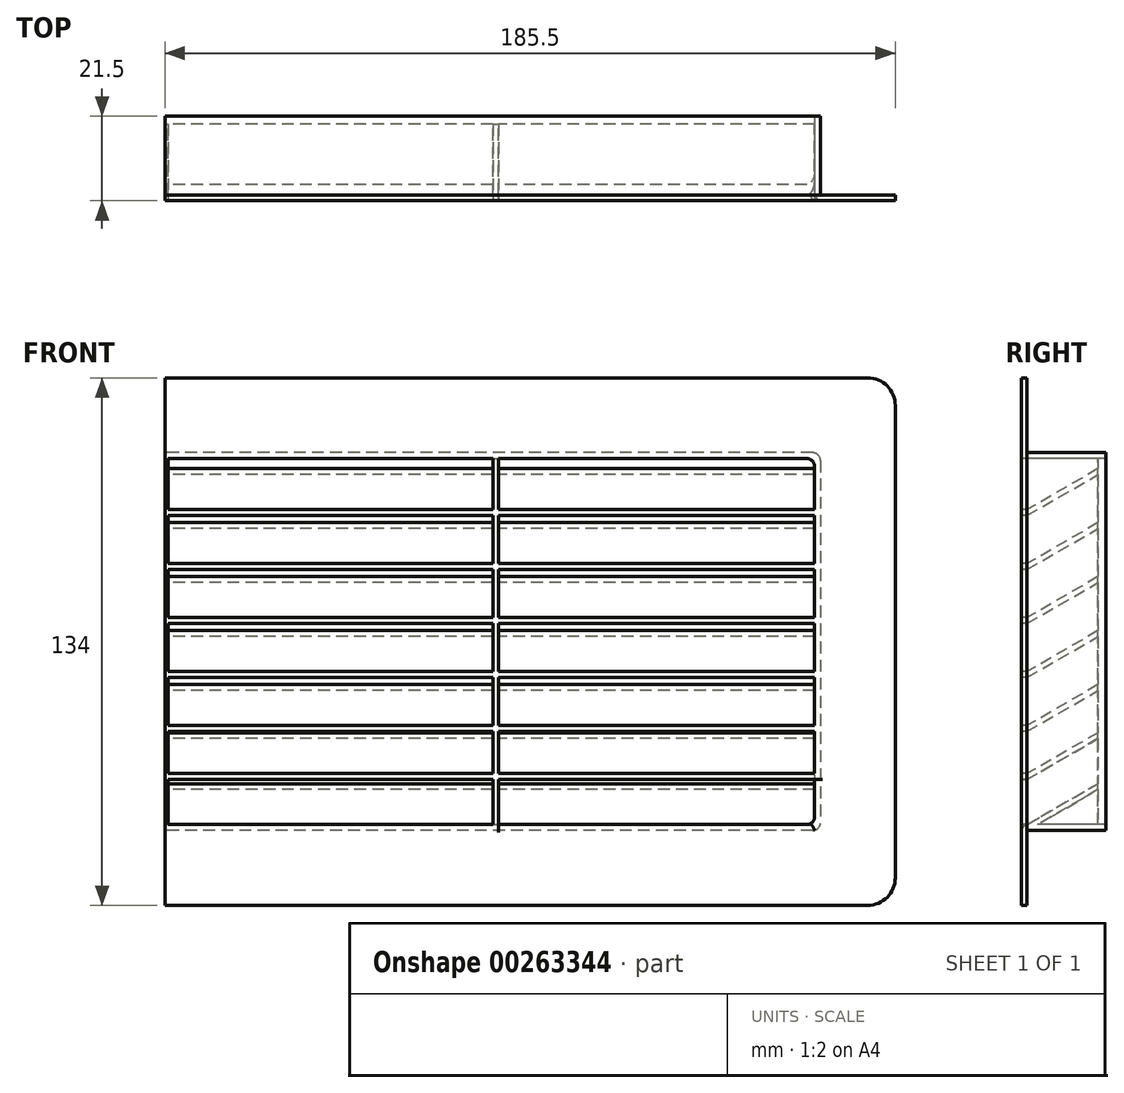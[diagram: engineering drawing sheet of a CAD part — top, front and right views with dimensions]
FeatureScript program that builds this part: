
annotation { "Feature Type Name" : "Feature", "Feature Type Description" : "" }
export const myFeature = defineFeature(function(context is Context, id is Id, definition is map)
    precondition{}
    {
        {
            var Q0;
            Q0=qCreatedBy(makeId("Front.planeOp"),FACE);
            var sketch = newSketch(context, id + "F0", { "sketchPlane" : qUnion([Q0])});
            skLineSegment(sketch, "E0.bottom", {"start": v(-180, 65) * mm, "end": v(180, 65) * mm});
            skLineSegment(sketch, "E0.top", {"start": v(-180, -65) * mm, "end": v(180, -65) * mm});
            skLineSegment(sketch, "E0.left", {"start": v(-185, 60) * mm, "end": v(-185, -60) * mm});
            skLineSegment(sketch, "E0.right", {"start": v(185, 60) * mm, "end": v(185, -60) * mm});
            skPoint(sketch, "E0.middle", {"position": v(0, 0) * mm});
            skPoint(sketch, "E1.visualSharp", {"position": v(-185, 65) * mm});
            skArc(sketch, "E1.filletArc", {"start": v(-180, 65) * mm, "mid": v(-183.54, 63.54) * mm, "end": v(-185, 60) * mm});
            skPoint(sketch, "E2.visualSharp", {"position": v(185, 65) * mm});
            skArc(sketch, "E2.filletArc", {"start": v(185, 60) * mm, "mid": v(183.54, 63.54) * mm, "end": v(180, 65) * mm});
            skPoint(sketch, "E3.visualSharp", {"position": v(185, -65) * mm});
            skArc(sketch, "E3.filletArc", {"start": v(180, -65) * mm, "mid": v(183.54, -63.54) * mm, "end": v(185, -60) * mm});
            skPoint(sketch, "E4.visualSharp", {"position": v(-185, -65) * mm});
            skArc(sketch, "E4.filletArc", {"start": v(-185, -60) * mm, "mid": v(-183.54, -63.54) * mm, "end": v(-180, -65) * mm});
            skSolve(sketch);
        }
        {
            var Q0;
            Q0=qSketchRegion(id+"F0",true);
            extrude(context, id + "F1", {"entities" : qUnion([Q0]), "depth" : 1.5 * mm});
        }
        {
            var Q0;
            Q0=makeQuery(id+"F1.opExtrude","CAP_FACE",FACE,{"disambiguationData":[OSD([sQuery(id+"F0.wireOp",EDGE,"E0.bottom"),sQuery(id+"F0.wireOp",EDGE,"E0.top"),sQuery(id+"F0.wireOp",EDGE,"E0.left"),sQuery(id+"F0.wireOp",EDGE,"E0.right")])],"isStart":false});
            var sketch = newSketch(context, id + "F2", { "sketchPlane" : qUnion([Q0])});
            skLineSegment(sketch, "E5.bottom", {"start": v(-166.5, 46.5) * mm, "end": v(-83.25, 46.5) * mm});
            skLineSegment(sketch, "E5.top", {"start": v(-166.5, -46.5) * mm, "end": v(-83.25, -46.5) * mm});
            skLineSegment(sketch, "E5.left", {"start": v(-166.5, 46.5) * mm, "end": v(-166.5, 33.54) * mm});
            skLineSegment(sketch, "E5.right", {"start": v(166.5, 46.5) * mm, "end": v(166.5, 33.54) * mm});
            skPoint(sketch, "E5.middle", {"position": v(0, 0) * mm});
            skLineSegment(sketch, "E6.0", {"start": v(-166.5, 32.04) * mm, "end": v(-83.25, 32.04) * mm});
            skLineSegment(sketch, "E7.0", {"start": v(-166.5, 18.32) * mm, "end": v(-83.25, 18.32) * mm});
            skLineSegment(sketch, "E8.0", {"start": v(-166.5, 4.6) * mm, "end": v(-83.25, 4.6) * mm});
            skLineSegment(sketch, "E9.0", {"start": v(-166.5, -9.1) * mm, "end": v(-83.25, -9.1) * mm});
            skLineSegment(sketch, "E10.0", {"start": v(-166.5, -22.82) * mm, "end": v(-83.25, -22.82) * mm});
            skLineSegment(sketch, "E11.0", {"start": v(-166.5, -33.54) * mm, "end": v(-83.25, -33.54) * mm});
            skLineSegment(sketch, "E12.0", {"start": v(-166.5, 33.54) * mm, "end": v(-83.25, 33.54) * mm});
            skLineSegment(sketch, "E13.0", {"start": v(-166.5, 19.82) * mm, "end": v(-83.25, 19.82) * mm});
            skLineSegment(sketch, "E14.0", {"start": v(-166.5, 6.1) * mm, "end": v(-83.25, 6.1) * mm});
            skLineSegment(sketch, "E15.0", {"start": v(-166.5, -7.6) * mm, "end": v(-83.25, -7.6) * mm});
            skLineSegment(sketch, "E16.0", {"start": v(-166.5, -21.32) * mm, "end": v(-83.25, -21.32) * mm});
            skLineSegment(sketch, "E17.0", {"start": v(-166.5, -35.04) * mm, "end": v(-83.25, -35.04) * mm});
            skLineSegment(sketch, "E18.0", {"start": v(-83.25, 46.5) * mm, "end": v(-83.25, 33.54) * mm});
            skLineSegment(sketch, "E19.0", {"start": v(-81.75, 46.5) * mm, "end": v(-81.75, 33.54) * mm});
            skLineSegment(sketch, "E20.0", {"start": v(0.75, 46.5) * mm, "end": v(0.75, 33.54) * mm});
            skLineSegment(sketch, "E21.0", {"start": v(2.25, 46.5) * mm, "end": v(2.25, 33.54) * mm});
            skLineSegment(sketch, "E22.0", {"start": v(84.75, 46.5) * mm, "end": v(84.75, 33.54) * mm});
            skLineSegment(sketch, "E23.0", {"start": v(86.25, 46.5) * mm, "end": v(86.25, 33.54) * mm});
            skLineSegment(sketch, "E24.trimOffspring", {"start": v(-81.75, 19.82) * mm, "end": v(0.75, 19.82) * mm});
            skLineSegment(sketch, "E25.trimOffspring", {"start": v(-81.75, 18.32) * mm, "end": v(0.75, 18.32) * mm});
            skLineSegment(sketch, "E26.trimOffspring", {"start": v(-81.75, 33.54) * mm, "end": v(0.75, 33.54) * mm});
            skLineSegment(sketch, "E27.trimOffspring", {"start": v(-81.75, 32.04) * mm, "end": v(0.75, 32.04) * mm});
            skLineSegment(sketch, "E28.trimOffspring", {"start": v(-83.25, 32.04) * mm, "end": v(-83.25, 19.82) * mm});
            skLineSegment(sketch, "E29.trimOffspring", {"start": v(-81.75, 32.04) * mm, "end": v(-81.75, 19.82) * mm});
            skLineSegment(sketch, "E30.trimOffspring", {"start": v(-166.5, 32.04) * mm, "end": v(-166.5, 19.82) * mm});
            skLineSegment(sketch, "E31.trimOffspring", {"start": v(-166.5, 18.32) * mm, "end": v(-166.5, 6.1) * mm});
            skLineSegment(sketch, "E32.trimOffspring", {"start": v(-81.75, 18.32) * mm, "end": v(-81.75, 6.1) * mm});
            skLineSegment(sketch, "E33.trimOffspring", {"start": v(-83.25, 18.32) * mm, "end": v(-83.25, 6.1) * mm});
            skLineSegment(sketch, "E34.trimOffspring", {"start": v(-83.25, 4.6) * mm, "end": v(-83.25, -7.6) * mm});
            skLineSegment(sketch, "E35.trimOffspring", {"start": v(-81.75, 4.6) * mm, "end": v(-81.75, -7.6) * mm});
            skLineSegment(sketch, "E36.trimOffspring", {"start": v(-81.75, 4.6) * mm, "end": v(0.75, 4.6) * mm});
            skLineSegment(sketch, "E37.trimOffspring", {"start": v(-81.75, 6.1) * mm, "end": v(0.75, 6.1) * mm});
            skLineSegment(sketch, "E38.trimOffspring", {"start": v(-166.5, 4.6) * mm, "end": v(-166.5, -7.6) * mm});
            skLineSegment(sketch, "E39.trimOffspring", {"start": v(-166.5, -9.1) * mm, "end": v(-166.5, -21.32) * mm});
            skLineSegment(sketch, "E40.trimOffspring", {"start": v(-83.25, -9.1) * mm, "end": v(-83.25, -21.32) * mm});
            skLineSegment(sketch, "E41.trimOffspring", {"start": v(-81.75, -9.1) * mm, "end": v(-81.75, -21.32) * mm});
            skLineSegment(sketch, "E42.trimOffspring", {"start": v(-81.75, -7.6) * mm, "end": v(0.75, -7.6) * mm});
            skLineSegment(sketch, "E43.trimOffspring", {"start": v(-81.75, -9.1) * mm, "end": v(0.75, -9.1) * mm});
            skLineSegment(sketch, "E44.trimOffspring", {"start": v(-166.5, -22.82) * mm, "end": v(-166.5, -33.54) * mm});
            skLineSegment(sketch, "E45.trimOffspring", {"start": v(-166.5, -35.04) * mm, "end": v(-166.5, -46.5) * mm});
            skLineSegment(sketch, "E46.trimOffspring", {"start": v(-83.25, -22.82) * mm, "end": v(-83.25, -33.54) * mm});
            skLineSegment(sketch, "E47.trimOffspring", {"start": v(-81.75, -22.82) * mm, "end": v(0.75, -22.82) * mm});
            skLineSegment(sketch, "E48.trimOffspring", {"start": v(-81.75, -21.32) * mm, "end": v(0.75, -21.32) * mm});
            skLineSegment(sketch, "E49.trimOffspring", {"start": v(-81.75, -22.82) * mm, "end": v(-81.75, -33.54) * mm});
            skLineSegment(sketch, "E50.trimOffspring", {"start": v(-83.25, -35.04) * mm, "end": v(-83.25, -46.5) * mm});
            skLineSegment(sketch, "E51.trimOffspring", {"start": v(-81.75, -35.04) * mm, "end": v(0.75, -35.04) * mm});
            skLineSegment(sketch, "E52.trimOffspring", {"start": v(-81.75, -33.54) * mm, "end": v(0.75, -33.54) * mm});
            skLineSegment(sketch, "E53.trimOffspring", {"start": v(-81.75, -35.04) * mm, "end": v(-81.75, -46.5) * mm});
            skLineSegment(sketch, "E54.trimOffspring", {"start": v(-81.75, -46.5) * mm, "end": v(0.75, -46.5) * mm});
            skLineSegment(sketch, "E55.trimOffspring", {"start": v(-81.75, 46.5) * mm, "end": v(0.75, 46.5) * mm});
            skLineSegment(sketch, "E56.trimOffspring", {"start": v(2.25, 46.5) * mm, "end": v(84.75, 46.5) * mm});
            skLineSegment(sketch, "E57.trimOffspring", {"start": v(2.25, 32.04) * mm, "end": v(84.75, 32.04) * mm});
            skLineSegment(sketch, "E58.trimOffspring", {"start": v(2.25, 33.54) * mm, "end": v(84.75, 33.54) * mm});
            skLineSegment(sketch, "E59.trimOffspring", {"start": v(2.25, 32.04) * mm, "end": v(2.25, 19.82) * mm});
            skLineSegment(sketch, "E60.trimOffspring", {"start": v(0.75, 32.04) * mm, "end": v(0.75, 19.82) * mm});
            skLineSegment(sketch, "E61.trimOffspring", {"start": v(2.25, 19.82) * mm, "end": v(84.75, 19.82) * mm});
            skLineSegment(sketch, "E62.trimOffspring", {"start": v(2.25, 18.32) * mm, "end": v(2.25, 6.1) * mm});
            skLineSegment(sketch, "E63.trimOffspring", {"start": v(2.25, 18.32) * mm, "end": v(84.75, 18.32) * mm});
            skLineSegment(sketch, "E64.trimOffspring", {"start": v(0.75, 18.32) * mm, "end": v(0.75, 6.1) * mm});
            skLineSegment(sketch, "E65.trimOffspring", {"start": v(2.25, 4.6) * mm, "end": v(2.25, -7.6) * mm});
            skLineSegment(sketch, "E66.trimOffspring", {"start": v(2.25, 6.1) * mm, "end": v(84.75, 6.1) * mm});
            skLineSegment(sketch, "E67.trimOffspring", {"start": v(0.75, 4.6) * mm, "end": v(0.75, -7.6) * mm});
            skLineSegment(sketch, "E68.trimOffspring", {"start": v(2.25, 4.6) * mm, "end": v(84.75, 4.6) * mm});
            skLineSegment(sketch, "E69.trimOffspring", {"start": v(2.25, -7.6) * mm, "end": v(84.75, -7.6) * mm});
            skLineSegment(sketch, "E70.trimOffspring", {"start": v(0.75, -9.1) * mm, "end": v(0.75, -21.32) * mm});
            skLineSegment(sketch, "E71.trimOffspring", {"start": v(2.25, -9.1) * mm, "end": v(2.25, -21.32) * mm});
            skLineSegment(sketch, "E72.trimOffspring", {"start": v(2.25, -9.1) * mm, "end": v(84.75, -9.1) * mm});
            skLineSegment(sketch, "E73.trimOffspring", {"start": v(2.25, -22.82) * mm, "end": v(2.25, -33.54) * mm});
            skLineSegment(sketch, "E74.trimOffspring", {"start": v(2.25, -21.32) * mm, "end": v(84.75, -21.32) * mm});
            skLineSegment(sketch, "E75.trimOffspring", {"start": v(0.75, -22.82) * mm, "end": v(0.75, -33.54) * mm});
            skLineSegment(sketch, "E76.trimOffspring", {"start": v(2.25, -22.82) * mm, "end": v(84.75, -22.82) * mm});
            skLineSegment(sketch, "E77.trimOffspring", {"start": v(2.25, -35.04) * mm, "end": v(84.75, -35.04) * mm});
            skLineSegment(sketch, "E78.trimOffspring", {"start": v(2.25, -35.04) * mm, "end": v(2.25, -46.5) * mm});
            skLineSegment(sketch, "E79.trimOffspring", {"start": v(2.25, -33.54) * mm, "end": v(84.75, -33.54) * mm});
            skLineSegment(sketch, "E80.trimOffspring", {"start": v(0.75, -35.04) * mm, "end": v(0.75, -46.5) * mm});
            skLineSegment(sketch, "E81.trimOffspring", {"start": v(2.25, -46.5) * mm, "end": v(84.75, -46.5) * mm});
            skLineSegment(sketch, "E82.trimOffspring", {"start": v(86.25, 46.5) * mm, "end": v(166.5, 46.5) * mm});
            skLineSegment(sketch, "E83.trimOffspring", {"start": v(86.25, 33.54) * mm, "end": v(166.5, 33.54) * mm});
            skLineSegment(sketch, "E84.trimOffspring", {"start": v(84.75, 32.04) * mm, "end": v(84.75, 19.82) * mm});
            skLineSegment(sketch, "E85.trimOffspring", {"start": v(86.25, 32.04) * mm, "end": v(86.25, 19.82) * mm});
            skLineSegment(sketch, "E86.trimOffspring", {"start": v(86.25, 32.04) * mm, "end": v(166.5, 32.04) * mm});
            skLineSegment(sketch, "E87.trimOffspring", {"start": v(84.75, 4.6) * mm, "end": v(84.75, -7.6) * mm});
            skLineSegment(sketch, "E88.trimOffspring", {"start": v(86.25, 4.6) * mm, "end": v(86.25, -7.6) * mm});
            skLineSegment(sketch, "E89.trimOffspring", {"start": v(86.25, 6.1) * mm, "end": v(166.5, 6.1) * mm});
            skLineSegment(sketch, "E90.trimOffspring", {"start": v(86.25, 4.6) * mm, "end": v(166.5, 4.6) * mm});
            skLineSegment(sketch, "E91.trimOffspring", {"start": v(86.25, 18.32) * mm, "end": v(166.5, 18.32) * mm});
            skLineSegment(sketch, "E92.trimOffspring", {"start": v(86.25, 18.32) * mm, "end": v(86.25, 6.1) * mm});
            skLineSegment(sketch, "E93.trimOffspring", {"start": v(84.75, 18.32) * mm, "end": v(84.75, 6.1) * mm});
            skLineSegment(sketch, "E94.trimOffspring", {"start": v(86.25, 19.82) * mm, "end": v(166.5, 19.82) * mm});
            skLineSegment(sketch, "E95.trimOffspring", {"start": v(86.25, -22.82) * mm, "end": v(166.5, -22.82) * mm});
            skLineSegment(sketch, "E96.trimOffspring", {"start": v(86.25, -22.82) * mm, "end": v(86.25, -33.54) * mm});
            skLineSegment(sketch, "E97.trimOffspring", {"start": v(84.75, -22.82) * mm, "end": v(84.75, -33.54) * mm});
            skLineSegment(sketch, "E98.trimOffspring", {"start": v(86.25, -9.1) * mm, "end": v(86.25, -21.32) * mm});
            skLineSegment(sketch, "E99.trimOffspring", {"start": v(84.75, -9.1) * mm, "end": v(84.75, -21.32) * mm});
            skLineSegment(sketch, "E100.trimOffspring", {"start": v(86.25, -7.6) * mm, "end": v(166.5, -7.6) * mm});
            skLineSegment(sketch, "E101.trimOffspring", {"start": v(86.25, -9.1) * mm, "end": v(166.5, -9.1) * mm});
            skLineSegment(sketch, "E102.trimOffspring", {"start": v(86.25, -21.32) * mm, "end": v(166.5, -21.32) * mm});
            skLineSegment(sketch, "E103.trimOffspring", {"start": v(86.25, -35.04) * mm, "end": v(86.25, -46.5) * mm});
            skLineSegment(sketch, "E104.trimOffspring", {"start": v(86.25, -35.04) * mm, "end": v(166.5, -35.04) * mm});
            skLineSegment(sketch, "E105.trimOffspring", {"start": v(86.25, -33.54) * mm, "end": v(166.5, -33.54) * mm});
            skLineSegment(sketch, "E106.trimOffspring", {"start": v(84.75, -35.04) * mm, "end": v(84.75, -46.5) * mm});
            skLineSegment(sketch, "E107.trimOffspring", {"start": v(86.25, -46.5) * mm, "end": v(166.5, -46.5) * mm});
            skLineSegment(sketch, "E108.trimOffspring", {"start": v(166.5, -35.04) * mm, "end": v(166.5, -46.5) * mm});
            skLineSegment(sketch, "E109.trimOffspring", {"start": v(166.5, -22.82) * mm, "end": v(166.5, -33.54) * mm});
            skLineSegment(sketch, "E110.trimOffspring", {"start": v(166.5, 32.04) * mm, "end": v(166.5, 19.82) * mm});
            skLineSegment(sketch, "E111.trimOffspring", {"start": v(166.5, 18.32) * mm, "end": v(166.5, 6.1) * mm});
            skLineSegment(sketch, "E112.trimOffspring", {"start": v(166.5, 4.6) * mm, "end": v(166.5, -7.6) * mm});
            skLineSegment(sketch, "E113.trimOffspring", {"start": v(166.5, -9.1) * mm, "end": v(166.5, -21.32) * mm});
            skSolve(sketch);
        }
        {
            var Q0;
            Q0=makeQuery(id+"F2.imprint","IMPRINT",FACE,{"disambiguationData":[TD([[makeQuery(id+"F2.imprint","IMPRINT",EDGE,{"derivedFrom":sQuery(id+"F2.wireOp",EDGE,"E5.bottom")}),-1.0]])]});
            var Q1;
            Q1=makeQuery(id+"F2.imprint","IMPRINT",FACE,{"disambiguationData":[TD([[makeQuery(id+"F2.imprint","IMPRINT",EDGE,{"derivedFrom":sQuery(id+"F2.wireOp",EDGE,"E19.0")}),1.0]])]});
            var Q2;
            Q2=makeQuery(id+"F2.imprint","IMPRINT",FACE,{"disambiguationData":[TD([[makeQuery(id+"F2.imprint","IMPRINT",EDGE,{"derivedFrom":sQuery(id+"F2.wireOp",EDGE,"E21.0")}),1.0]])]});
            var Q3;
            Q3=makeQuery(id+"F2.imprint","IMPRINT",FACE,{"disambiguationData":[TD([[makeQuery(id+"F2.imprint","IMPRINT",EDGE,{"derivedFrom":sQuery(id+"F2.wireOp",EDGE,"E5.right")}),-1.0]])]});
            var Q4;
            Q4=makeQuery(id+"F2.imprint","IMPRINT",FACE,{"disambiguationData":[TD([[makeQuery(id+"F2.imprint","IMPRINT",EDGE,{"derivedFrom":sQuery(id+"F2.wireOp",EDGE,"E6.0")}),-1.0]])]});
            var Q5;
            Q5=makeQuery(id+"F2.imprint","IMPRINT",FACE,{"disambiguationData":[TD([[makeQuery(id+"F2.imprint","IMPRINT",EDGE,{"derivedFrom":sQuery(id+"F2.wireOp",EDGE,"E24.trimOffspring")}),1.0]])]});
            var Q6;
            Q6=makeQuery(id+"F2.imprint","IMPRINT",FACE,{"disambiguationData":[TD([[makeQuery(id+"F2.imprint","IMPRINT",EDGE,{"derivedFrom":sQuery(id+"F2.wireOp",EDGE,"E57.trimOffspring")}),-1.0]])]});
            var Q7;
            Q7=makeQuery(id+"F2.imprint","IMPRINT",FACE,{"disambiguationData":[TD([[makeQuery(id+"F2.imprint","IMPRINT",EDGE,{"derivedFrom":sQuery(id+"F2.wireOp",EDGE,"E85.trimOffspring")}),1.0]])]});
            var Q8;
            Q8=makeQuery(id+"F2.imprint","IMPRINT",FACE,{"disambiguationData":[TD([[makeQuery(id+"F2.imprint","IMPRINT",EDGE,{"derivedFrom":sQuery(id+"F2.wireOp",EDGE,"E7.0")}),-1.0]])]});
            var Q9;
            Q9=makeQuery(id+"F2.imprint","IMPRINT",FACE,{"disambiguationData":[TD([[makeQuery(id+"F2.imprint","IMPRINT",EDGE,{"derivedFrom":sQuery(id+"F2.wireOp",EDGE,"E25.trimOffspring")}),-1.0]])]});
            var Q10;
            Q10=makeQuery(id+"F2.imprint","IMPRINT",FACE,{"disambiguationData":[TD([[makeQuery(id+"F2.imprint","IMPRINT",EDGE,{"derivedFrom":sQuery(id+"F2.wireOp",EDGE,"E62.trimOffspring")}),1.0]])]});
            var Q11;
            Q11=makeQuery(id+"F2.imprint","IMPRINT",FACE,{"disambiguationData":[TD([[makeQuery(id+"F2.imprint","IMPRINT",EDGE,{"derivedFrom":sQuery(id+"F2.wireOp",EDGE,"E89.trimOffspring")}),1.0]])]});
            var Q12;
            Q12=makeQuery(id+"F2.imprint","IMPRINT",FACE,{"disambiguationData":[TD([[makeQuery(id+"F2.imprint","IMPRINT",EDGE,{"derivedFrom":sQuery(id+"F2.wireOp",EDGE,"E8.0")}),-1.0]])]});
            var Q13;
            Q13=makeQuery(id+"F2.imprint","IMPRINT",FACE,{"disambiguationData":[TD([[makeQuery(id+"F2.imprint","IMPRINT",EDGE,{"derivedFrom":sQuery(id+"F2.wireOp",EDGE,"E35.trimOffspring")}),1.0]])]});
            var Q14;
            Q14=makeQuery(id+"F2.imprint","IMPRINT",FACE,{"disambiguationData":[TD([[makeQuery(id+"F2.imprint","IMPRINT",EDGE,{"derivedFrom":sQuery(id+"F2.wireOp",EDGE,"E65.trimOffspring")}),1.0]])]});
            var Q15;
            Q15=makeQuery(id+"F2.imprint","IMPRINT",FACE,{"disambiguationData":[TD([[makeQuery(id+"F2.imprint","IMPRINT",EDGE,{"derivedFrom":sQuery(id+"F2.wireOp",EDGE,"E88.trimOffspring")}),1.0]])]});
            var Q16;
            Q16=makeQuery(id+"F2.imprint","IMPRINT",FACE,{"disambiguationData":[TD([[makeQuery(id+"F2.imprint","IMPRINT",EDGE,{"derivedFrom":sQuery(id+"F2.wireOp",EDGE,"E9.0")}),-1.0]])]});
            var Q17;
            Q17=makeQuery(id+"F2.imprint","IMPRINT",FACE,{"disambiguationData":[TD([[makeQuery(id+"F2.imprint","IMPRINT",EDGE,{"derivedFrom":sQuery(id+"F2.wireOp",EDGE,"E41.trimOffspring")}),1.0]])]});
            var Q18;
            Q18=makeQuery(id+"F2.imprint","IMPRINT",FACE,{"disambiguationData":[TD([[makeQuery(id+"F2.imprint","IMPRINT",EDGE,{"derivedFrom":sQuery(id+"F2.wireOp",EDGE,"E71.trimOffspring")}),1.0]])]});
            var Q19;
            Q19=makeQuery(id+"F2.imprint","IMPRINT",FACE,{"disambiguationData":[TD([[makeQuery(id+"F2.imprint","IMPRINT",EDGE,{"derivedFrom":sQuery(id+"F2.wireOp",EDGE,"E98.trimOffspring")}),1.0]])]});
            var Q20;
            Q20=makeQuery(id+"F2.imprint","IMPRINT",FACE,{"disambiguationData":[TD([[makeQuery(id+"F2.imprint","IMPRINT",EDGE,{"derivedFrom":sQuery(id+"F2.wireOp",EDGE,"E10.0")}),-1.0]])]});
            var Q21;
            Q21=makeQuery(id+"F2.imprint","IMPRINT",FACE,{"disambiguationData":[TD([[makeQuery(id+"F2.imprint","IMPRINT",EDGE,{"derivedFrom":sQuery(id+"F2.wireOp",EDGE,"E47.trimOffspring")}),-1.0]])]});
            var Q22;
            Q22=makeQuery(id+"F2.imprint","IMPRINT",FACE,{"disambiguationData":[TD([[makeQuery(id+"F2.imprint","IMPRINT",EDGE,{"derivedFrom":sQuery(id+"F2.wireOp",EDGE,"E73.trimOffspring")}),1.0]])]});
            var Q23;
            Q23=makeQuery(id+"F2.imprint","IMPRINT",FACE,{"disambiguationData":[TD([[makeQuery(id+"F2.imprint","IMPRINT",EDGE,{"derivedFrom":sQuery(id+"F2.wireOp",EDGE,"E95.trimOffspring")}),-1.0]])]});
            var Q24;
            Q24=makeQuery(id+"F2.imprint","IMPRINT",FACE,{"disambiguationData":[TD([[makeQuery(id+"F2.imprint","IMPRINT",EDGE,{"derivedFrom":sQuery(id+"F2.wireOp",EDGE,"E5.top")}),1.0]])]});
            var Q25;
            Q25=makeQuery(id+"F2.imprint","IMPRINT",FACE,{"disambiguationData":[TD([[makeQuery(id+"F2.imprint","IMPRINT",EDGE,{"derivedFrom":sQuery(id+"F2.wireOp",EDGE,"E51.trimOffspring")}),-1.0]])]});
            var Q26;
            Q26=makeQuery(id+"F2.imprint","IMPRINT",FACE,{"disambiguationData":[TD([[makeQuery(id+"F2.imprint","IMPRINT",EDGE,{"derivedFrom":sQuery(id+"F2.wireOp",EDGE,"E77.trimOffspring")}),-1.0]])]});
            var Q27;
            Q27=makeQuery(id+"F2.imprint","IMPRINT",FACE,{"disambiguationData":[TD([[makeQuery(id+"F2.imprint","IMPRINT",EDGE,{"derivedFrom":sQuery(id+"F2.wireOp",EDGE,"E103.trimOffspring")}),1.0]])]});
            extrude(context, id + "F3", {"entities" : qUnion([Q0, Q1, Q2, Q3, Q4, Q5, Q6, Q7, Q8, Q9, Q10, Q11, Q12, Q13, Q14, Q15, Q16, Q17, Q18, Q19, Q20, Q21, Q22, Q23, Q24, Q25, Q26, Q27]), "operationType" : NewBodyOperationType.REMOVE, "endBound" : BoundingType.THROUGH_ALL, "oppositeDirection" : true, "depth" : 25 * mm});
        }
        {
            var Q0;
            Q0=makeQuery(id+"F1.opExtrude","CAP_FACE",FACE,{"disambiguationData":[OSD([sQuery(id+"F0.wireOp",EDGE,"E0.bottom"),sQuery(id+"F0.wireOp",EDGE,"E0.top"),sQuery(id+"F0.wireOp",EDGE,"E0.left"),sQuery(id+"F0.wireOp",EDGE,"E0.right")])],"isStart":true});
            var sketch = newSketch(context, id + "F4", { "sketchPlane" : qUnion([Q0])});
            skLineSegment(sketch, "E114.bottom", {"start": v(-166.5, 46.5) * mm, "end": v(166.5, 46.5) * mm});
            skLineSegment(sketch, "E114.top", {"start": v(-166.5, -46.5) * mm, "end": v(166.5, -46.5) * mm});
            skLineSegment(sketch, "E114.left", {"start": v(-166.5, 46.5) * mm, "end": v(-166.5, -46.5) * mm});
            skLineSegment(sketch, "E114.right", {"start": v(166.5, 46.5) * mm, "end": v(166.5, -46.5) * mm});
            skPoint(sketch, "E114.middle", {"position": v(0, 0) * mm});
            skLineSegment(sketch, "E115.0", {"start": v(-168, 48) * mm, "end": v(168, 48) * mm});
            skLineSegment(sketch, "E115.1", {"start": v(-168, 48) * mm, "end": v(-168, -48) * mm});
            skLineSegment(sketch, "E115.2", {"start": v(-168, -48) * mm, "end": v(168, -48) * mm});
            skLineSegment(sketch, "E115.3", {"start": v(168, 48) * mm, "end": v(168, -48) * mm});
            skSolve(sketch);
        }
        {
            var Q0;
            Q0=qSketchRegion(id+"F4",true);
            extrude(context, id + "F5", {"entities" : qUnion([Q0]), "operationType" : NewBodyOperationType.ADD, "depth" : 20 * mm});
        }
        {
            var Q0;
            Q0=makeQuery(id+"F5.boolean.opBoolean","MERGE",FACE,{"derivedFrom":[makeQuery(id+"F3.boolean.opBoolean","COPY",FACE,{"derivedFrom":makeQuery(id+"F3.opExtrude","SWEPT_FACE",FACE,{"disambiguationData":[OSD([sQuery(id+"F2.wireOp",EDGE,"E5.left")])]})}),makeQuery(id+"F3.boolean.opBoolean","COPY",FACE,{"derivedFrom":makeQuery(id+"F3.opExtrude","SWEPT_FACE",FACE,{"disambiguationData":[OSD([sQuery(id+"F2.wireOp",EDGE,"E30.trimOffspring")])]})}),makeQuery(id+"F3.boolean.opBoolean","COPY",FACE,{"derivedFrom":makeQuery(id+"F3.opExtrude","SWEPT_FACE",FACE,{"disambiguationData":[OSD([sQuery(id+"F2.wireOp",EDGE,"E31.trimOffspring")])]})}),makeQuery(id+"F3.boolean.opBoolean","COPY",FACE,{"derivedFrom":makeQuery(id+"F3.opExtrude","SWEPT_FACE",FACE,{"disambiguationData":[OSD([sQuery(id+"F2.wireOp",EDGE,"E38.trimOffspring")])]})}),makeQuery(id+"F3.boolean.opBoolean","COPY",FACE,{"derivedFrom":makeQuery(id+"F3.opExtrude","SWEPT_FACE",FACE,{"disambiguationData":[OSD([sQuery(id+"F2.wireOp",EDGE,"E39.trimOffspring")])]})}),makeQuery(id+"F3.boolean.opBoolean","COPY",FACE,{"derivedFrom":makeQuery(id+"F3.opExtrude","SWEPT_FACE",FACE,{"disambiguationData":[OSD([sQuery(id+"F2.wireOp",EDGE,"E44.trimOffspring")])]})}),makeQuery(id+"F3.boolean.opBoolean","COPY",FACE,{"derivedFrom":makeQuery(id+"F3.opExtrude","SWEPT_FACE",FACE,{"disambiguationData":[OSD([sQuery(id+"F2.wireOp",EDGE,"E45.trimOffspring")])]})}),makeQuery(id+"F5.opExtrude","SWEPT_FACE",FACE,{"disambiguationData":[OSD([sQuery(id+"F4.wireOp",EDGE,"E114.right")])]})]});
            var sketch = newSketch(context, id + "F6", { "sketchPlane" : qUnion([Q0])});
            skLineSegment(sketch, "E116", {"start": v(0, 46.5) * mm, "end": v(0, -35.04) * mm, "construction": true});
            skPoint(sketch, "E116.endSnap0", {"position": v(0, 19.07) * mm});
            skLineSegment(sketch, "E117", {"start": v(0, 33.54) * mm, "end": v(18, 43.93) * mm});
            skLineSegment(sketch, "E118", {"start": v(18, 43.93) * mm, "end": v(18, 42.43) * mm});
            skLineSegment(sketch, "E119", {"start": v(18, 42.43) * mm, "end": v(0, 32.04) * mm});
            skLineSegment(sketch, "E120", {"start": v(0, 32.04) * mm, "end": v(0, 33.54) * mm});
            skLineSegment(sketch, "E121", {"start": v(0, 33.54) * mm, "end": v(0, 32.04) * mm});
            skLineSegment(sketch, "E122.0.1.0", {"start": v(0, 19.82) * mm, "end": v(18, 30.21) * mm});
            skLineSegment(sketch, "E122.0.1.1", {"start": v(18, 28.71) * mm, "end": v(0, 18.32) * mm});
            skLineSegment(sketch, "E122.0.1.2", {"start": v(18, 30.21) * mm, "end": v(18, 28.71) * mm});
            skLineSegment(sketch, "E122.0.2.0", {"start": v(0, 6.1) * mm, "end": v(18, 16.5) * mm});
            skLineSegment(sketch, "E122.0.2.1", {"start": v(18, 15) * mm, "end": v(0, 4.6) * mm});
            skLineSegment(sketch, "E122.0.2.2", {"start": v(18, 16.5) * mm, "end": v(18, 15) * mm});
            skLineSegment(sketch, "E122.0.3.0", {"start": v(0, -7.6) * mm, "end": v(18, 2.79) * mm});
            skLineSegment(sketch, "E122.0.3.1", {"start": v(18, 1.29) * mm, "end": v(0, -9.1) * mm});
            skLineSegment(sketch, "E122.0.3.2", {"start": v(18, 2.79) * mm, "end": v(18, 1.29) * mm});
            skLineSegment(sketch, "E122.0.4.0", {"start": v(0, -21.32) * mm, "end": v(18, -10.93) * mm});
            skLineSegment(sketch, "E122.0.4.1", {"start": v(18, -12.43) * mm, "end": v(0, -22.82) * mm});
            skLineSegment(sketch, "E122.0.4.2", {"start": v(18, -10.93) * mm, "end": v(18, -12.43) * mm});
            skLineSegment(sketch, "E122.0.5.0", {"start": v(0, -35.04) * mm, "end": v(18, -24.64) * mm});
            skLineSegment(sketch, "E122.direction1", {"start": v(0, 33.54) * mm, "end": v(0, 33.54) * mm});
            skLineSegment(sketch, "E122.direction2", {"start": v(0, 33.54) * mm, "end": v(0, 19.82) * mm, "construction": true});
            skLineSegment(sketch, "E123", {"start": v(0, 19.82) * mm, "end": v(0, 18.32) * mm});
            skLineSegment(sketch, "E124", {"start": v(0, 6.1) * mm, "end": v(0, 4.6) * mm});
            skLineSegment(sketch, "E125", {"start": v(0, -33.54) * mm, "end": v(18, -23.14) * mm});
            skLineSegment(sketch, "E126", {"start": v(18, -23.14) * mm, "end": v(18, -24.64) * mm});
            skLineSegment(sketch, "E127.trimOffspring", {"start": v(0, -35.04) * mm, "end": v(0, -46.5) * mm, "construction": true});
            skLineSegment(sketch, "E128", {"start": v(0, -35.04) * mm, "end": v(0, -33.54) * mm});
            skLineSegment(sketch, "E129", {"start": v(0, -21.32) * mm, "end": v(0, -22.82) * mm});
            skLineSegment(sketch, "E130", {"start": v(0, -46.5) * mm, "end": v(18, -36.1) * mm});
            skLineSegment(sketch, "E131", {"start": v(18, -36.1) * mm, "end": v(18, -37.6) * mm});
            skLineSegment(sketch, "E132", {"start": v(18, -37.6) * mm, "end": v(2.6, -46.5) * mm});
            skLineSegment(sketch, "E133", {"start": v(2.6, -46.5) * mm, "end": v(0, -46.5) * mm});
            skLineSegment(sketch, "E134", {"start": v(0, -7.6) * mm, "end": v(0, -9.1) * mm});
            skSolve(sketch);
        }
        {
            var Q0;
            Q0=makeQuery(id+"F5.boolean.opBoolean","SPLIT",FACE,{"disambiguationData":[TD([makeQuery(id+"F3.boolean.opBoolean","COPY",FACE,{"derivedFrom":makeQuery(id+"F3.opExtrude","SWEPT_FACE",FACE,{"disambiguationData":[OSD([sQuery(id+"F2.wireOp",EDGE,"E5.bottom")])]})})])],"derivedFrom":makeQuery(id+"F1.opExtrude","CAP_FACE",FACE,{"disambiguationData":[OSD([sQuery(id+"F0.wireOp",EDGE,"E0.bottom"),sQuery(id+"F0.wireOp",EDGE,"E0.top"),sQuery(id+"F0.wireOp",EDGE,"E0.left"),sQuery(id+"F0.wireOp",EDGE,"E0.right")])],"isStart":true})});
            var sketch = newSketch(context, id + "F7", { "sketchPlane" : qUnion([Q0])});
            skLineSegment(sketch, "E135.bottom", {"start": v(-86.25, 46.5) * mm, "end": v(-84.75, 46.5) * mm});
            skLineSegment(sketch, "E135.top", {"start": v(-86.25, -46.5) * mm, "end": v(-84.75, -46.5) * mm});
            skLineSegment(sketch, "E135.left", {"start": v(-86.25, 46.5) * mm, "end": v(-86.25, -46.5) * mm});
            skLineSegment(sketch, "E135.right", {"start": v(-84.75, 46.5) * mm, "end": v(-84.75, -46.5) * mm});
            skLineSegment(sketch, "E136.bottom", {"start": v(-2.25, 46.5) * mm, "end": v(-0.75, 46.5) * mm});
            skLineSegment(sketch, "E136.top", {"start": v(-2.25, -46.5) * mm, "end": v(-0.75, -46.5) * mm});
            skLineSegment(sketch, "E136.left", {"start": v(-2.25, 46.5) * mm, "end": v(-2.25, -46.5) * mm});
            skLineSegment(sketch, "E136.right", {"start": v(-0.75, 46.5) * mm, "end": v(-0.75, -46.5) * mm});
            skLineSegment(sketch, "E137.bottom", {"start": v(81.75, 46.5) * mm, "end": v(83.25, 46.5) * mm});
            skLineSegment(sketch, "E137.top", {"start": v(81.75, -46.5) * mm, "end": v(83.25, -46.5) * mm});
            skLineSegment(sketch, "E137.left", {"start": v(81.75, 46.5) * mm, "end": v(81.75, -46.5) * mm});
            skLineSegment(sketch, "E137.right", {"start": v(83.25, 46.5) * mm, "end": v(83.25, -46.5) * mm});
            skSolve(sketch);
        }
        {
            var Q0;
            Q0=qSketchRegion(id+"F7",true);
            extrude(context, id + "F8", {"entities" : qUnion([Q0]), "operationType" : NewBodyOperationType.ADD, "depth" : 18 * mm});
        }
        {
            var Q0;
            Q0=qSketchRegion(id+"F6",true);
            var Q1;
            Q1=makeQuery(id+"F5.boolean.opBoolean","MERGE",FACE,{"derivedFrom":[makeQuery(id+"F3.boolean.opBoolean","COPY",FACE,{"derivedFrom":makeQuery(id+"F3.opExtrude","SWEPT_FACE",FACE,{"disambiguationData":[OSD([sQuery(id+"F2.wireOp",EDGE,"E5.right")])]})}),makeQuery(id+"F3.boolean.opBoolean","COPY",FACE,{"derivedFrom":makeQuery(id+"F3.opExtrude","SWEPT_FACE",FACE,{"disambiguationData":[OSD([sQuery(id+"F2.wireOp",EDGE,"E108.trimOffspring")])]})}),makeQuery(id+"F3.boolean.opBoolean","COPY",FACE,{"derivedFrom":makeQuery(id+"F3.opExtrude","SWEPT_FACE",FACE,{"disambiguationData":[OSD([sQuery(id+"F2.wireOp",EDGE,"E109.trimOffspring")])]})}),makeQuery(id+"F3.boolean.opBoolean","COPY",FACE,{"derivedFrom":makeQuery(id+"F3.opExtrude","SWEPT_FACE",FACE,{"disambiguationData":[OSD([sQuery(id+"F2.wireOp",EDGE,"E110.trimOffspring")])]})}),makeQuery(id+"F3.boolean.opBoolean","COPY",FACE,{"derivedFrom":makeQuery(id+"F3.opExtrude","SWEPT_FACE",FACE,{"disambiguationData":[OSD([sQuery(id+"F2.wireOp",EDGE,"E111.trimOffspring")])]})}),makeQuery(id+"F3.boolean.opBoolean","COPY",FACE,{"derivedFrom":makeQuery(id+"F3.opExtrude","SWEPT_FACE",FACE,{"disambiguationData":[OSD([sQuery(id+"F2.wireOp",EDGE,"E112.trimOffspring")])]})}),makeQuery(id+"F3.boolean.opBoolean","COPY",FACE,{"derivedFrom":makeQuery(id+"F3.opExtrude","SWEPT_FACE",FACE,{"disambiguationData":[OSD([sQuery(id+"F2.wireOp",EDGE,"E113.trimOffspring")])]})}),makeQuery(id+"F5.opExtrude","SWEPT_FACE",FACE,{"disambiguationData":[OSD([sQuery(id+"F4.wireOp",EDGE,"E114.left")])]})]});
            extrude(context, id + "F9", {"entities" : qUnion([Q0]), "operationType" : NewBodyOperationType.ADD, "endBound" : BoundingType.UP_TO_SURFACE, "endBoundEntityFace" : qUnion([Q1]), "depth" : 25 * mm});
        }
        {
            var Q0;
            Q0=makeQuery(id+"F5.opExtrude","SWEPT_EDGE",EDGE,{"disambiguationData":[OSD([sQuery(id+"F4.wireOp",EDGE,"E115.1"),sQuery(id+"F4.wireOp",EDGE,"E115.2")])]});
            var Q1;
            Q1=makeQuery(id+"F5.opExtrude","SWEPT_EDGE",EDGE,{"disambiguationData":[OSD([sQuery(id+"F4.wireOp",EDGE,"E115.0"),sQuery(id+"F4.wireOp",EDGE,"E115.1")])]});
            var Q2;
            Q2=makeQuery(id+"F5.opExtrude","SWEPT_EDGE",EDGE,{"disambiguationData":[OSD([sQuery(id+"F4.wireOp",EDGE,"E115.2"),sQuery(id+"F4.wireOp",EDGE,"E115.3")])]});
            var Q3;
            Q3=makeQuery(id+"F5.opExtrude","SWEPT_EDGE",EDGE,{"disambiguationData":[OSD([sQuery(id+"F4.wireOp",EDGE,"E115.0"),sQuery(id+"F4.wireOp",EDGE,"E115.3")])]});
            fillet(context, id + "F10", {"entities" : qUnion([Q0, Q1, Q2, Q3]), "radius" : 2 * mm, "tangentPropagation" : true, "allowEdgeOverflow" : false});
        }
        {
            var Q0;
            Q0=makeQuery(id+"F5.boolean.opBoolean","MERGE",EDGE,{"derivedFrom":[makeQuery(id+"F3.boolean.opBoolean","COPY",EDGE,{"derivedFrom":makeQuery(id+"F3.opExtrude","SWEPT_EDGE",EDGE,{"disambiguationData":[OSD([sQuery(id+"F2.wireOp",EDGE,"E5.bottom"),sQuery(id+"F2.wireOp",EDGE,"E5.left")])]})}),makeQuery(id+"F5.opExtrude","SWEPT_EDGE",EDGE,{"disambiguationData":[OSD([sQuery(id+"F4.wireOp",EDGE,"E114.bottom"),sQuery(id+"F4.wireOp",EDGE,"E114.right")])]})]});
            fillet(context, id + "F11", {"entities" : qUnion([Q0]), "radius" : 2 * mm, "tangentPropagation" : true, "allowEdgeOverflow" : false});
        }
        {
            var Q0;
            {var subQ0=sQuery(id+"F2.wireOp",EDGE,"E45.trimOffspring");var subQ1=sQuery(id+"F2.wireOp",EDGE,"E5.top");var subQ2=sQuery(id+"F4.wireOp",EDGE,"E114.right");var subQ3=sQuery(id+"F4.wireOp",EDGE,"E114.top");Q0=makeQuery(id+"F9.boolean.opBoolean","SPLIT",EDGE,{"disambiguationData":[TD([makeQuery(id+"F9.opExtrude","SWEPT_FACE",FACE,{"disambiguationData":[OSD([sQuery(id+"F6.wireOp",EDGE,"E132")])]})])],"derivedFrom":makeQuery(id+"F5.boolean.opBoolean","MERGE",EDGE,{"derivedFrom":[makeQuery(id+"F3.boolean.opBoolean","COPY",EDGE,{"derivedFrom":makeQuery(id+"F3.opExtrude","SWEPT_EDGE",EDGE,{"disambiguationData":[OSD([subQ1,subQ0])]})}),makeQuery(id+"F5.opExtrude","SWEPT_EDGE",EDGE,{"disambiguationData":[OSD([subQ3,subQ2])]})]})});}
            var Q1;
            {var subQ0=sQuery(id+"F2.wireOp",EDGE,"E108.trimOffspring");var subQ1=sQuery(id+"F2.wireOp",EDGE,"E107.trimOffspring");var subQ2=sQuery(id+"F4.wireOp",EDGE,"E114.left");var subQ3=sQuery(id+"F4.wireOp",EDGE,"E114.top");Q1=makeQuery(id+"F9.boolean.opBoolean","SPLIT",EDGE,{"disambiguationData":[TD([makeQuery(id+"F9.opExtrude","SWEPT_FACE",FACE,{"disambiguationData":[OSD([sQuery(id+"F6.wireOp",EDGE,"E132")])]})])],"derivedFrom":makeQuery(id+"F5.boolean.opBoolean","MERGE",EDGE,{"derivedFrom":[makeQuery(id+"F3.boolean.opBoolean","COPY",EDGE,{"derivedFrom":makeQuery(id+"F3.opExtrude","SWEPT_EDGE",EDGE,{"disambiguationData":[OSD([subQ1,subQ0])]})}),makeQuery(id+"F5.opExtrude","SWEPT_EDGE",EDGE,{"disambiguationData":[OSD([subQ3,subQ2])]})]})});}
            var Q2;
            Q2=makeQuery(id+"F5.boolean.opBoolean","MERGE",EDGE,{"derivedFrom":[makeQuery(id+"F3.boolean.opBoolean","COPY",EDGE,{"derivedFrom":makeQuery(id+"F3.opExtrude","SWEPT_EDGE",EDGE,{"disambiguationData":[OSD([sQuery(id+"F2.wireOp",EDGE,"E5.right"),sQuery(id+"F2.wireOp",EDGE,"E82.trimOffspring")])]})}),makeQuery(id+"F5.opExtrude","SWEPT_EDGE",EDGE,{"disambiguationData":[OSD([sQuery(id+"F4.wireOp",EDGE,"E114.bottom"),sQuery(id+"F4.wireOp",EDGE,"E114.left")])]})]});
            fillet(context, id + "F12", {"entities" : qUnion([Q0, Q1, Q2]), "radius" : 2 * mm, "tangentPropagation" : true, "allowEdgeOverflow" : false});
        }
        {
            var Q0;
            {var subQ0=sQuery(id+"F2.wireOp",EDGE,"E45.trimOffspring");var subQ1=sQuery(id+"F4.wireOp",EDGE,"E114.right");var subQ2=sQuery(id+"F2.wireOp",EDGE,"E5.top");var subQ3=sQuery(id+"F4.wireOp",EDGE,"E114.top");Q0=makeQuery(id+"F9.boolean.opBoolean","SPLIT",EDGE,{"disambiguationData":[TD([makeQuery(id+"F9.opExtrude","SWEPT_FACE",FACE,{"disambiguationData":[OSD([sQuery(id+"F6.wireOp",EDGE,"E130")])]})])],"derivedFrom":makeQuery(id+"F5.boolean.opBoolean","MERGE",EDGE,{"derivedFrom":[makeQuery(id+"F3.boolean.opBoolean","COPY",EDGE,{"derivedFrom":makeQuery(id+"F3.opExtrude","SWEPT_EDGE",EDGE,{"disambiguationData":[OSD([subQ2,subQ0])]})}),makeQuery(id+"F5.opExtrude","SWEPT_EDGE",EDGE,{"disambiguationData":[OSD([subQ3,subQ1])]})]})});}
            var Q1;
            {var subQ0=sQuery(id+"F2.wireOp",EDGE,"E108.trimOffspring");var subQ1=sQuery(id+"F2.wireOp",EDGE,"E107.trimOffspring");var subQ2=sQuery(id+"F4.wireOp",EDGE,"E114.top");var subQ3=sQuery(id+"F4.wireOp",EDGE,"E114.left");Q1=makeQuery(id+"F9.boolean.opBoolean","SPLIT",EDGE,{"disambiguationData":[TD([makeQuery(id+"F9.opExtrude","SWEPT_FACE",FACE,{"disambiguationData":[OSD([sQuery(id+"F6.wireOp",EDGE,"E130")])]})])],"derivedFrom":makeQuery(id+"F5.boolean.opBoolean","MERGE",EDGE,{"derivedFrom":[makeQuery(id+"F3.boolean.opBoolean","COPY",EDGE,{"derivedFrom":makeQuery(id+"F3.opExtrude","SWEPT_EDGE",EDGE,{"disambiguationData":[OSD([subQ1,subQ0])]})}),makeQuery(id+"F5.opExtrude","SWEPT_EDGE",EDGE,{"disambiguationData":[OSD([subQ2,subQ3])]})]})});}
            fillet(context, id + "F13", {"entities" : qUnion([Q0, Q1]), "radius" : 2 * mm, "tangentPropagation" : true, "allowEdgeOverflow" : false});
        }
        {
            var Q0;
            Q0=makeQuery(id+"F3.boolean.opBoolean","COPY",EDGE,{"derivedFrom":makeQuery(id+"F3.opExtrude","CAP_EDGE",EDGE,{"disambiguationData":[OSD([sQuery(id+"F2.wireOp",EDGE,"E55.trimOffspring")])],"isStart":true})});
            var Q1;
            Q1=makeQuery(id+"F3.boolean.opBoolean","COPY",EDGE,{"derivedFrom":makeQuery(id+"F3.opExtrude","CAP_EDGE",EDGE,{"disambiguationData":[OSD([sQuery(id+"F2.wireOp",EDGE,"E56.trimOffspring")])],"isStart":true})});
            var Q2;
            Q2=makeQuery(id+"F3.boolean.opBoolean","COPY",EDGE,{"derivedFrom":makeQuery(id+"F3.opExtrude","CAP_EDGE",EDGE,{"disambiguationData":[OSD([sQuery(id+"F2.wireOp",EDGE,"E82.trimOffspring")])],"isStart":true})});
            var Q3;
            Q3=makeQuery(id+"F3.boolean.opBoolean","COPY",EDGE,{"derivedFrom":makeQuery(id+"F3.opExtrude","CAP_EDGE",EDGE,{"disambiguationData":[OSD([sQuery(id+"F2.wireOp",EDGE,"E110.trimOffspring")])],"isStart":true})});
            var Q4;
            Q4=makeQuery(id+"F3.boolean.opBoolean","COPY",EDGE,{"derivedFrom":makeQuery(id+"F3.opExtrude","CAP_EDGE",EDGE,{"disambiguationData":[OSD([sQuery(id+"F2.wireOp",EDGE,"E111.trimOffspring")])],"isStart":true})});
            var Q5;
            Q5=makeQuery(id+"F3.boolean.opBoolean","COPY",EDGE,{"derivedFrom":makeQuery(id+"F3.opExtrude","CAP_EDGE",EDGE,{"disambiguationData":[OSD([sQuery(id+"F2.wireOp",EDGE,"E112.trimOffspring")])],"isStart":true})});
            var Q6;
            Q6=makeQuery(id+"F3.boolean.opBoolean","COPY",EDGE,{"derivedFrom":makeQuery(id+"F3.opExtrude","CAP_EDGE",EDGE,{"disambiguationData":[OSD([sQuery(id+"F2.wireOp",EDGE,"E113.trimOffspring")])],"isStart":true})});
            var Q7;
            Q7=makeQuery(id+"F3.boolean.opBoolean","COPY",EDGE,{"derivedFrom":makeQuery(id+"F3.opExtrude","CAP_EDGE",EDGE,{"disambiguationData":[OSD([sQuery(id+"F2.wireOp",EDGE,"E109.trimOffspring")])],"isStart":true})});
            var Q8;
            Q8=makeQuery(id+"F3.boolean.opBoolean","COPY",EDGE,{"derivedFrom":makeQuery(id+"F3.opExtrude","CAP_EDGE",EDGE,{"disambiguationData":[OSD([sQuery(id+"F2.wireOp",EDGE,"E108.trimOffspring")])],"isStart":true})});
            var Q9;
            {var subQ0=makeQuery(id+"F1.opExtrude","CAP_FACE",FACE,{"disambiguationData":[OSD([sQuery(id+"F0.wireOp",EDGE,"E0.bottom"),sQuery(id+"F0.wireOp",EDGE,"E0.top"),sQuery(id+"F0.wireOp",EDGE,"E0.left"),sQuery(id+"F0.wireOp",EDGE,"E0.right"),sQuery(id+"F0.wireOp",EDGE,"E1.filletArc"),sQuery(id+"F0.wireOp",EDGE,"E2.filletArc"),sQuery(id+"F0.wireOp",EDGE,"E3.filletArc"),sQuery(id+"F0.wireOp",EDGE,"E4.filletArc")])],"isStart":false});var subQ1=sQuery(id+"F2.wireOp",EDGE,"E108.trimOffspring");var subQ2=sQuery(id+"F2.wireOp",EDGE,"E107.trimOffspring");var subQ3=sQuery(id+"F4.wireOp",EDGE,"E114.top");var subQ4=sQuery(id+"F4.wireOp",EDGE,"E114.left");Q9=makeQuery(id+"F13.opFillet","BLEND_EDGE",EDGE,{"blendedFrom":[makeQuery(id+"F9.boolean.opBoolean","SPLIT",EDGE,{"disambiguationData":[TD([makeQuery(id+"F9.opExtrude","SWEPT_FACE",FACE,{"disambiguationData":[OSD([sQuery(id+"F6.wireOp",EDGE,"E130")])]})])],"derivedFrom":makeQuery(id+"F5.boolean.opBoolean","MERGE",EDGE,{"derivedFrom":[makeQuery(id+"F3.boolean.opBoolean","COPY",EDGE,{"derivedFrom":makeQuery(id+"F3.opExtrude","SWEPT_EDGE",EDGE,{"disambiguationData":[OSD([subQ2,subQ1])]})}),makeQuery(id+"F5.opExtrude","SWEPT_EDGE",EDGE,{"disambiguationData":[OSD([subQ3,subQ4])]})]})}),subQ0],"blendedInto":[subQ0]});}
            var Q10;
            Q10=makeQuery(id+"F3.boolean.opBoolean","COPY",EDGE,{"derivedFrom":makeQuery(id+"F3.opExtrude","CAP_EDGE",EDGE,{"disambiguationData":[OSD([sQuery(id+"F2.wireOp",EDGE,"E81.trimOffspring")])],"isStart":true})});
            var Q11;
            Q11=makeQuery(id+"F3.boolean.opBoolean","COPY",EDGE,{"derivedFrom":makeQuery(id+"F3.opExtrude","CAP_EDGE",EDGE,{"disambiguationData":[OSD([sQuery(id+"F2.wireOp",EDGE,"E54.trimOffspring")])],"isStart":true})});
            var Q12;
            Q12=makeQuery(id+"F3.boolean.opBoolean","COPY",EDGE,{"derivedFrom":makeQuery(id+"F3.opExtrude","CAP_EDGE",EDGE,{"disambiguationData":[OSD([sQuery(id+"F2.wireOp",EDGE,"E5.top")])],"isStart":true})});
            var Q13;
            Q13=makeQuery(id+"F3.boolean.opBoolean","COPY",EDGE,{"derivedFrom":makeQuery(id+"F3.opExtrude","CAP_EDGE",EDGE,{"disambiguationData":[OSD([sQuery(id+"F2.wireOp",EDGE,"E44.trimOffspring")])],"isStart":true})});
            var Q14;
            Q14=makeQuery(id+"F3.boolean.opBoolean","COPY",EDGE,{"derivedFrom":makeQuery(id+"F3.opExtrude","CAP_EDGE",EDGE,{"disambiguationData":[OSD([sQuery(id+"F2.wireOp",EDGE,"E39.trimOffspring")])],"isStart":true})});
            var Q15;
            Q15=makeQuery(id+"F3.boolean.opBoolean","COPY",EDGE,{"derivedFrom":makeQuery(id+"F3.opExtrude","CAP_EDGE",EDGE,{"disambiguationData":[OSD([sQuery(id+"F2.wireOp",EDGE,"E38.trimOffspring")])],"isStart":true})});
            var Q16;
            Q16=makeQuery(id+"F3.boolean.opBoolean","COPY",EDGE,{"derivedFrom":makeQuery(id+"F3.opExtrude","CAP_EDGE",EDGE,{"disambiguationData":[OSD([sQuery(id+"F2.wireOp",EDGE,"E31.trimOffspring")])],"isStart":true})});
            var Q17;
            Q17=makeQuery(id+"F3.boolean.opBoolean","COPY",EDGE,{"derivedFrom":makeQuery(id+"F3.opExtrude","CAP_EDGE",EDGE,{"disambiguationData":[OSD([sQuery(id+"F2.wireOp",EDGE,"E30.trimOffspring")])],"isStart":true})});
            var Q18;
            Q18=makeQuery(id+"F3.boolean.opBoolean","COPY",EDGE,{"derivedFrom":makeQuery(id+"F3.opExtrude","CAP_EDGE",EDGE,{"disambiguationData":[OSD([sQuery(id+"F2.wireOp",EDGE,"E5.left")])],"isStart":true})});
            fillet(context, id + "F14", {"entities" : qUnion([Q0, Q1, Q2, Q3, Q4, Q5, Q6, Q7, Q8, Q9, Q10, Q11, Q12, Q13, Q14, Q15, Q16, Q17, Q18]), "radius" : 2 * mm, "tangentPropagation" : true, "allowEdgeOverflow" : false});
        }
        {
            var Q0;
            Q0=makeQuery(id+"F1.opExtrude","CAP_FACE",FACE,{"disambiguationData":[OSD([sQuery(id+"F0.wireOp",EDGE,"E0.bottom"),sQuery(id+"F0.wireOp",EDGE,"E0.top"),sQuery(id+"F0.wireOp",EDGE,"E0.left"),sQuery(id+"F0.wireOp",EDGE,"E0.right"),sQuery(id+"F0.wireOp",EDGE,"E1.filletArc"),sQuery(id+"F0.wireOp",EDGE,"E2.filletArc"),sQuery(id+"F0.wireOp",EDGE,"E3.filletArc"),sQuery(id+"F0.wireOp",EDGE,"E4.filletArc")])],"isStart":false});
            var sketch = newSketch(context, id + "F15", { "sketchPlane" : qUnion([Q0])});
            skLineSegment(sketch, "E138.0", {"start": v(-180, 65) * mm, "end": v(180, 65) * mm});
            skLineSegment(sketch, "E139.0", {"start": v(-185, 60) * mm, "end": v(-185, -60) * mm});
            skArc(sketch, "E140.0", {"start": v(-180, 65) * mm, "mid": v(-183.54, 63.54) * mm, "end": v(-185, 60) * mm});
            skArc(sketch, "E141.0", {"start": v(-185, -60) * mm, "mid": v(-183.54, -63.54) * mm, "end": v(-180, -65) * mm});
            skLineSegment(sketch, "E142.0", {"start": v(-180, -65) * mm, "end": v(180, -65) * mm});
            skArc(sketch, "E143.0", {"start": v(180, -65) * mm, "mid": v(183.54, -63.54) * mm, "end": v(185, -60) * mm});
            skLineSegment(sketch, "E144.0", {"start": v(185, 60) * mm, "end": v(185, -60) * mm});
            skArc(sketch, "E145.0", {"start": v(-180, 67) * mm, "mid": v(-184.95, 64.95) * mm, "end": v(-187, 60) * mm});
            skLineSegment(sketch, "E145.1", {"start": v(-187, 60) * mm, "end": v(-187, -60) * mm});
            skLineSegment(sketch, "E145.2", {"start": v(-180, 67) * mm, "end": v(180, 67) * mm});
            skArc(sketch, "E145.3", {"start": v(-187, -60) * mm, "mid": v(-184.95, -64.95) * mm, "end": v(-180, -67) * mm});
            skArc(sketch, "E145.4", {"start": v(187, 60) * mm, "mid": v(184.95, 64.95) * mm, "end": v(180, 67) * mm});
            skLineSegment(sketch, "E145.5", {"start": v(187, 60) * mm, "end": v(187, -60) * mm});
            skArc(sketch, "E145.6", {"start": v(180, -67) * mm, "mid": v(184.95, -64.95) * mm, "end": v(187, -60) * mm});
            skLineSegment(sketch, "E145.7", {"start": v(-180, -67) * mm, "end": v(180, -67) * mm});
            skSolve(sketch);
        }
        {
            var Q0;
            Q0=makeQuery(id+"F15.imprint","IMPRINT",FACE,{"disambiguationData":[TD([[makeQuery(id+"F15.imprint","IMPRINT",EDGE,{"derivedFrom":sQuery(id+"F15.wireOp",EDGE,"E138.0")}),1.0]])]});
            extrude(context, id + "F16", {"entities" : qUnion([Q0]), "oppositeDirection" : true, "depth" : 1.5 * mm, "offsetDistance" : 25 * mm});
        }
        {
            var Q0;
            Q0=makeQuery(id+"F1.opExtrude","SWEPT_BODY",BODY,{"disambiguationData":[OSD([sQuery(id+"F0.wireOp",EDGE,"E0.bottom"),sQuery(id+"F0.wireOp",EDGE,"E0.top"),sQuery(id+"F0.wireOp",EDGE,"E0.left"),sQuery(id+"F0.wireOp",EDGE,"E0.right"),sQuery(id+"F0.wireOp",EDGE,"E1.filletArc"),sQuery(id+"F0.wireOp",EDGE,"E2.filletArc"),sQuery(id+"F0.wireOp",EDGE,"E3.filletArc"),sQuery(id+"F0.wireOp",EDGE,"E4.filletArc")])]});
            var Q1;
            Q1=makeQuery(id+"F16.opExtrude","SWEPT_BODY",BODY,{"disambiguationData":[OSD([sQuery(id+"F0.wireOp",EDGE,"E2.filletArc"),sQuery(id+"F15.wireOp",EDGE,"E138.0"),sQuery(id+"F15.wireOp",EDGE,"E139.0"),sQuery(id+"F15.wireOp",EDGE,"E140.0"),sQuery(id+"F15.wireOp",EDGE,"E141.0"),sQuery(id+"F15.wireOp",EDGE,"E142.0"),sQuery(id+"F15.wireOp",EDGE,"E143.0"),sQuery(id+"F15.wireOp",EDGE,"E144.0"),sQuery(id+"F15.wireOp",EDGE,"E145.0"),sQuery(id+"F15.wireOp",EDGE,"E145.1"),sQuery(id+"F15.wireOp",EDGE,"E145.2"),sQuery(id+"F15.wireOp",EDGE,"E145.3"),sQuery(id+"F15.wireOp",EDGE,"E145.4"),sQuery(id+"F15.wireOp",EDGE,"E145.5"),sQuery(id+"F15.wireOp",EDGE,"E145.6"),sQuery(id+"F15.wireOp",EDGE,"E145.7")])]});
            booleanBodies(context, id + "F17", {"operationType" : BooleanOperationType.UNION, "tools" : qUnion([Q0, Q1])});
        }
        {
            var Q0;
            Q0=makeQuery(id+"F9.boolean.opBoolean","MERGE",FACE,{"derivedFrom":[makeQuery(id+"F8.opExtrude","CAP_FACE",FACE,{"disambiguationData":[OSD([sQuery(id+"F7.wireOp",EDGE,"E135.bottom"),sQuery(id+"F7.wireOp",EDGE,"E135.top"),sQuery(id+"F7.wireOp",EDGE,"E135.left"),sQuery(id+"F7.wireOp",EDGE,"E135.right")])],"isStart":false}),makeQuery(id+"F8.opExtrude","CAP_FACE",FACE,{"disambiguationData":[OSD([sQuery(id+"F7.wireOp",EDGE,"E136.bottom"),sQuery(id+"F7.wireOp",EDGE,"E136.top"),sQuery(id+"F7.wireOp",EDGE,"E136.left"),sQuery(id+"F7.wireOp",EDGE,"E136.right")])],"isStart":false}),makeQuery(id+"F8.opExtrude","CAP_FACE",FACE,{"disambiguationData":[OSD([sQuery(id+"F7.wireOp",EDGE,"E137.bottom"),sQuery(id+"F7.wireOp",EDGE,"E137.top"),sQuery(id+"F7.wireOp",EDGE,"E137.left"),sQuery(id+"F7.wireOp",EDGE,"E137.right")])],"isStart":false}),makeQuery(id+"F9.opExtrude","SWEPT_FACE",FACE,{"disambiguationData":[OSD([sQuery(id+"F6.wireOp",EDGE,"E118")])]}),makeQuery(id+"F9.opExtrude","SWEPT_FACE",FACE,{"disambiguationData":[OSD([sQuery(id+"F6.wireOp",EDGE,"E122.0.1.2")])]}),makeQuery(id+"F9.opExtrude","SWEPT_FACE",FACE,{"disambiguationData":[OSD([sQuery(id+"F6.wireOp",EDGE,"E122.0.2.2")])]}),makeQuery(id+"F9.opExtrude","SWEPT_FACE",FACE,{"disambiguationData":[OSD([sQuery(id+"F6.wireOp",EDGE,"E122.0.3.2")])]}),makeQuery(id+"F9.opExtrude","SWEPT_FACE",FACE,{"disambiguationData":[OSD([sQuery(id+"F6.wireOp",EDGE,"E122.0.4.2")])]}),makeQuery(id+"F9.opExtrude","SWEPT_FACE",FACE,{"disambiguationData":[OSD([sQuery(id+"F6.wireOp",EDGE,"E126")])]}),makeQuery(id+"F9.opExtrude","SWEPT_FACE",FACE,{"disambiguationData":[OSD([sQuery(id+"F6.wireOp",EDGE,"E131")])]})]});
            var sketch = newSketch(context, id + "F18", { "sketchPlane" : qUnion([Q0])});
            skLineSegment(sketch, "E146", {"start": v(-1.5, 46.5) * mm, "end": v(-1.5, -46.5) * mm, "construction": true});
            skLineSegment(sketch, "E147.left", {"start": v(-1.5, -67.78) * mm, "end": v(-1.5, 67) * mm});
            skLineSegment(sketch, "E148.0", {"start": v(180, 67) * mm, "end": v(-1.5, 67) * mm});
            skArc(sketch, "E149.0", {"start": v(180, 67) * mm, "mid": v(184.95, 64.95) * mm, "end": v(187, 60) * mm});
            skLineSegment(sketch, "E150.0", {"start": v(187, 60) * mm, "end": v(187, -60) * mm});
            skArc(sketch, "E151.0", {"start": v(187, -60) * mm, "mid": v(184.95, -64.95) * mm, "end": v(180, -67) * mm});
            skLineSegment(sketch, "E152.0", {"start": v(180, -67) * mm, "end": v(-1.5, -67) * mm});
            skPoint(sketch, "E153.orphan", {"position": v(-180, 67) * mm});
            skPoint(sketch, "E154.orphan", {"position": v(-180, -67) * mm});
            skSolve(sketch);
        }
        {
            var Q0;
            Q0 = qSketchRegion(id + "F18", true);
            extrude(context, id + "F19", {"entities" : qUnion([Q0]), "operationType" : NewBodyOperationType.REMOVE, "endBound" : BoundingType.THROUGH_ALL, "oppositeDirection" : true, "depth" : 25 * mm, "offsetDistance" : 25 * mm});
        }
        {
            var Q0;
            Q0=makeQuery(id+"F19.boolean.opBoolean","COPY",FACE,{"derivedFrom":makeQuery(id+"F19.opExtrude","CAP_FACE",FACE,{"disambiguationData":[OSD([sQuery(id+"F18.wireOp",EDGE,"E147.left"),sQuery(id+"F18.wireOp",EDGE,"E148.0"),sQuery(id+"F18.wireOp",EDGE,"E149.0"),sQuery(id+"F18.wireOp",EDGE,"E150.0"),sQuery(id+"F18.wireOp",EDGE,"E151.0"),sQuery(id+"F18.wireOp",EDGE,"E152.0")])],"isStart":true})});
            var sketch = newSketch(context, id + "F20", { "sketchPlane" : qUnion([Q0])});
            skLineSegment(sketch, "E155", {"start": v(1.5, -46.5) * mm, "end": v(1.5, -48) * mm});
            skLineSegment(sketch, "E156", {"start": v(1.5, -48) * mm, "end": v(-166, -48) * mm});
            skPoint(sketch, "E157.0", {"position": v(-167.41, -47.41) * mm});
            skArc(sketch, "E158.0", {"start": v(-168, -46) * mm, "mid": v(-167.41, -47.41) * mm, "end": v(-166, -48) * mm});
            skLineSegment(sketch, "E159.0", {"start": v(-168, 46) * mm, "end": v(-168, -46) * mm});
            skLineSegment(sketch, "E160.0", {"start": v(-164.5, -46.5) * mm, "end": v(1.5, -46.5) * mm});
            skLineSegment(sketch, "E161.0", {"start": v(-166.5, 44.5) * mm, "end": v(-166.5, -44.5) * mm});
            skArc(sketch, "E162.0", {"start": v(-166.5, -44.5) * mm, "mid": v(-165.91, -45.91) * mm, "end": v(-164.5, -46.5) * mm});
            skArc(sketch, "E163.0", {"start": v(-164.5, 46.5) * mm, "mid": v(-165.91, 45.91) * mm, "end": v(-166.5, 44.5) * mm});
            skArc(sketch, "E164.0", {"start": v(-166, 48) * mm, "mid": v(-167.41, 47.41) * mm, "end": v(-168, 46) * mm});
            skLineSegment(sketch, "E165.0", {"start": v(1.5, 48) * mm, "end": v(-166, 48) * mm});
            skLineSegment(sketch, "E166.0", {"start": v(1.5, 46.5) * mm, "end": v(1.5, 48) * mm});
            skLineSegment(sketch, "E167.0", {"start": v(-164.5, 46.5) * mm, "end": v(1.5, 46.5) * mm});
            skLineSegment(sketch, "E168.0.0", {"start": v(1.5, -46.5) * mm, "end": v(-164.5, -46.5) * mm});
            skLineSegment(sketch, "E168.0.2", {"start": v(-166.5, -44.5) * mm, "end": v(-166.5, 44.5) * mm});
            skLineSegment(sketch, "E168.0.10", {"start": v(-166, -48) * mm, "end": v(1.5, -48) * mm});
            skLineSegment(sketch, "E168.0.11", {"start": v(1.5, -48) * mm, "end": v(1.5, -46.5) * mm});
            skSolve(sketch);
        }
        {
            var Q0;
            Q0 = qSketchRegion(id + "F20", true);
            extrude(context, id + "F21", {"entities" : qUnion([Q0]), "operationType" : NewBodyOperationType.REMOVE, "endBound" : BoundingType.THROUGH_ALL, "oppositeDirection" : true, "depth" : 25 * mm, "offsetDistance" : 25 * mm});
        }
    });
